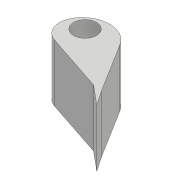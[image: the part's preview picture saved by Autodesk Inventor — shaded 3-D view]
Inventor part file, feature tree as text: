
AUTODESK INVENTOR PART (.ipt)
format: ipt  version: 2017 (Build 210142000, 142)  size: 110,592 bytes
history: native  units: mm
features: fillet x4, extrude x3, sketch x2
ambient origin geometry x8: Origin, YZ Plane, XZ Plane, XY Plane, X Axis, Y Axis, Z Axis, Center Point
bodies: Solid1 (feature_tree)
feature tree (9):
  sketch  "Sketch1"  dims[d0=4.0mm d1=21.0mm d2=10.0mm d3=0.0mm d4=4.75mm d5=4.75mm d6=4.75mm]
  extrude  "Extrusion1"  Depth=4.75mm
  fillet  "Fillet1"  Radius=10.0mm
  fillet  "Fillet2"  Radius=4.75mm
  fillet  "Fillet3"  Radius=4.75mm
  fillet  "Fillet6"  Radius=4.75mm
  extrude  "Extrusion2"  Depth=10.0mm TaperAngle=0.0deg
  extrude  "Extrusion3"  Depth=10.0mm
  sketch  "Sketch2"  dims[d9=3.25mm d10=11.5mm d11=0.0mm d12=3.0mm d13=10.0mm d14=0.0mm]
